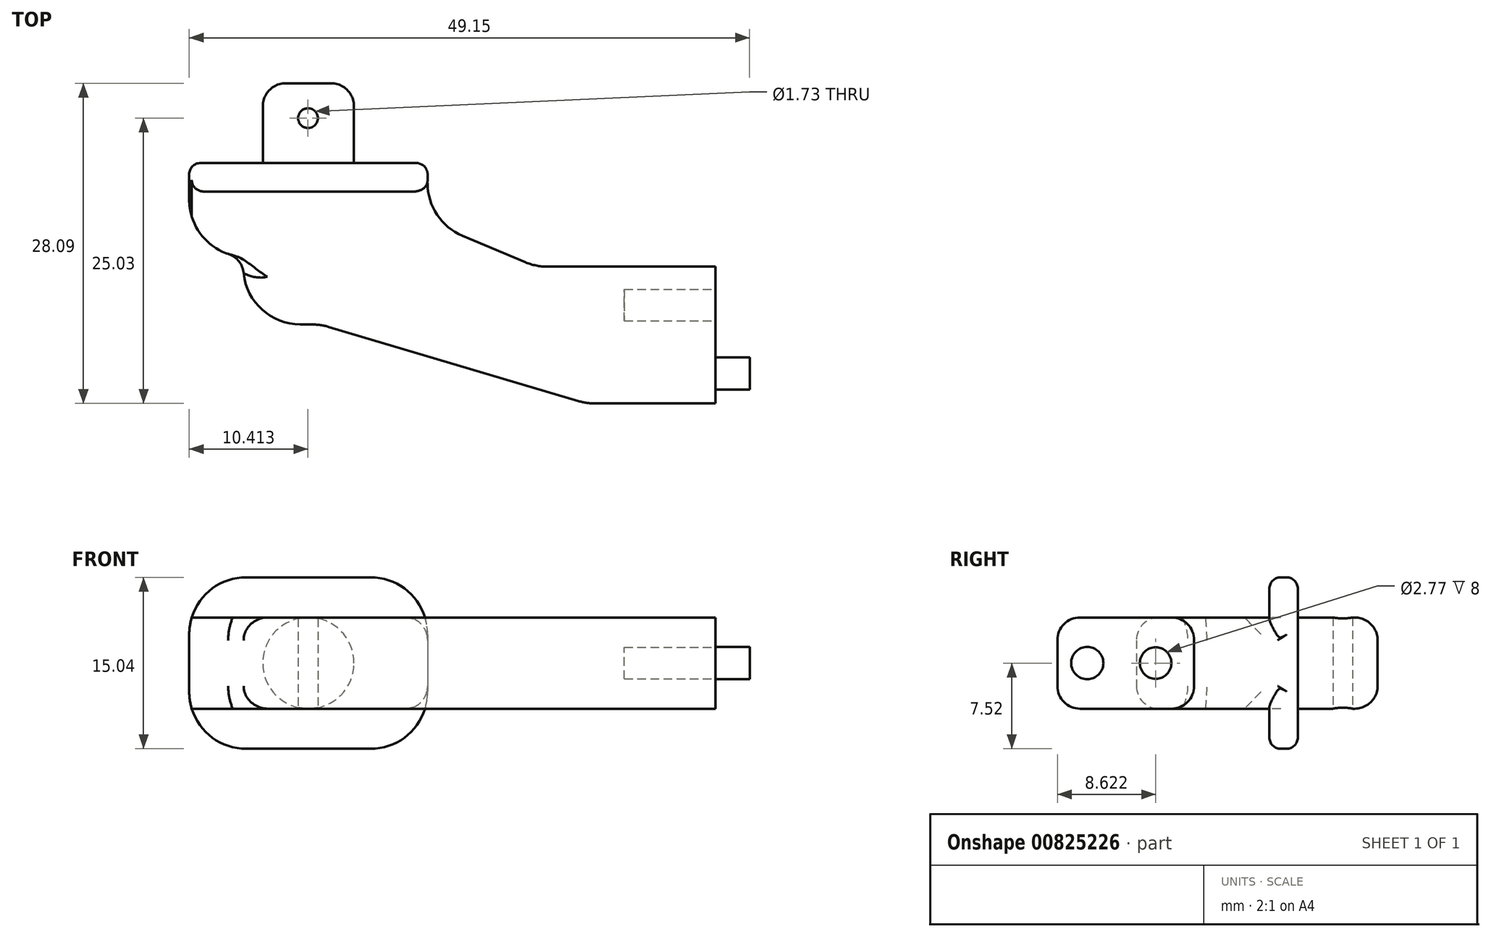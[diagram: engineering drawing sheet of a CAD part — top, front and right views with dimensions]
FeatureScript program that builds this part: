
annotation { "Feature Type Name" : "Feature", "Feature Type Description" : "" }
export const myFeature = defineFeature(function(context is Context, id is Id, definition is map)
    precondition{}
    {
        {
            var Q0;
            Q0=qCreatedBy(makeId("Top.planeOp"),FACE);
            var sketch = newSketch(context, id + "F0", { "sketchPlane" : qUnion([Q0])});
            skLineSegment(sketch, "E0.bottom", {"start": v(-29.76, 0) * mm, "end": v(-61.26, 0) * mm});
            skLineSegment(sketch, "E0.top", {"start": v(-29.76, 12) * mm, "end": v(-45.5, 12) * mm});
            skLineSegment(sketch, "E0.left", {"start": v(-29.76, 0) * mm, "end": v(-29.76, 12) * mm});
            skLineSegment(sketch, "E1", {"start": v(-61.26, 6) * mm, "end": v(-41.05, 0) * mm});
            skLineSegment(sketch, "E2", {"start": v(-45.5, 12) * mm, "end": v(-55, 16) * mm});
            skLineSegment(sketch, "E3", {"start": v(-75.91, 16) * mm, "end": v(-75.91, 12.87) * mm});
            skLineSegment(sketch, "E4", {"start": v(-75.91, 12.87) * mm, "end": v(-71.16, 12.87) * mm});
            skPoint(sketch, "E5.orphan", {"position": v(-61.26, 12) * mm});
            skLineSegment(sketch, "E6", {"start": v(-61.26, 6) * mm, "end": v(-64.38, 6.93) * mm});
            skLineSegment(sketch, "E7", {"start": v(-64.38, 6.93) * mm, "end": v(-71.16, 6.93) * mm});
            skLineSegment(sketch, "E8", {"start": v(-71.16, 6.93) * mm, "end": v(-71.16, 12.87) * mm});
            skLineSegment(sketch, "E9.top", {"start": v(-75.91, 21.1) * mm, "end": v(-55, 21.1) * mm});
            skLineSegment(sketch, "E9.left", {"start": v(-75.91, 16) * mm, "end": v(-75.91, 21.1) * mm});
            skLineSegment(sketch, "E9.right", {"start": v(-55, 16) * mm, "end": v(-55, 21.1) * mm});
            skPoint(sketch, "E10.end.orphan", {"position": v(-64.38, 6.34) * mm});
            skSolve(sketch);
        }
        {
            var Q0;
            Q0=makeQuery(id+"F0.imprint","IMPRINT",FACE,{"disambiguationData":[TD([[makeQuery(id+"F0.imprint","IMPRINT",EDGE,{"derivedFrom":sQuery(id+"F0.wireOp",EDGE,"E0.top")}),1.0]])]});
            extrude(context, id + "F1", {"entities" : qUnion([Q0]), "depth" : 8 * mm, "offsetDistance" : 25 * mm});
        }
        {
            var Q0;
            Q0=makeQuery(id+"F1.opExtrude","SWEPT_EDGE",EDGE,{"disambiguationData":[OSD([sQuery(id+"F0.wireOp",EDGE,"E3"),sQuery(id+"F0.wireOp",EDGE,"E4")])]});
            var Q1;
            Q1=makeQuery(id+"F1.opExtrude","SWEPT_EDGE",EDGE,{"disambiguationData":[OSD([sQuery(id+"F0.wireOp",EDGE,"E2"),sQuery(id+"F0.wireOp",EDGE,"E9.right")])]});
            var Q2;
            Q2=makeQuery(id+"F1.opExtrude","SWEPT_EDGE",EDGE,{"disambiguationData":[OSD([sQuery(id+"F0.wireOp",EDGE,"E0.top"),sQuery(id+"F0.wireOp",EDGE,"E2")])]});
            var Q3;
            Q3=makeQuery(id+"F1.opExtrude","SWEPT_EDGE",EDGE,{"disambiguationData":[OSD([sQuery(id+"F0.wireOp",EDGE,"E6"),sQuery(id+"F0.wireOp",EDGE,"E7")])]});
            var Q4;
            Q4=makeQuery(id+"F1.opExtrude","SWEPT_EDGE",EDGE,{"disambiguationData":[OSD([sQuery(id+"F0.wireOp",EDGE,"E0.bottom"),sQuery(id+"F0.wireOp",EDGE,"E1")])]});
            var Q5;
            Q5=makeQuery(id+"F1.opExtrude","SWEPT_EDGE",EDGE,{"disambiguationData":[OSD([sQuery(id+"F0.wireOp",EDGE,"E7"),sQuery(id+"F0.wireOp",EDGE,"E8")])]});
            fillet(context, id + "F2", {"entities" : qUnion([Q0, Q1, Q2, Q3, Q4, Q5]), "radius" : 5 * mm, "tangentPropagation" : true, "allowEdgeOverflow" : false});
        }
        {
            var Q0;
            Q0=makeQuery(id+"F1.opExtrude","SWEPT_FACE",FACE,{"disambiguationData":[OSD([sQuery(id+"F0.wireOp",EDGE,"E9.top")])]});
            var sketch = newSketch(context, id + "F3", { "sketchPlane" : qUnion([Q0])});
            skLineSegment(sketch, "E11.bottom", {"start": v(55, 8) * mm, "end": v(75.91, 8) * mm});
            skLineSegment(sketch, "E11.top", {"start": v(55, 11.52) * mm, "end": v(75.91, 11.52) * mm});
            skLineSegment(sketch, "E11.left", {"start": v(55, 8) * mm, "end": v(55, 11.52) * mm});
            skLineSegment(sketch, "E11.right", {"start": v(75.91, 8) * mm, "end": v(75.91, 11.52) * mm});
            skLineSegment(sketch, "E12.bottom", {"start": v(75.91, 0) * mm, "end": v(55, 0) * mm});
            skLineSegment(sketch, "E12.top", {"start": v(75.91, -3.52) * mm, "end": v(55, -3.52) * mm});
            skLineSegment(sketch, "E12.left", {"start": v(75.91, 0) * mm, "end": v(75.91, -3.52) * mm});
            skLineSegment(sketch, "E12.right", {"start": v(55, 0) * mm, "end": v(55, -3.52) * mm});
            skSolve(sketch);
        }
        {
            var Q0;
            Q0 = qSketchRegion(id + "F3", true);
            extrude(context, id + "F4", {"entities" : qUnion([Q0]), "operationType" : NewBodyOperationType.ADD, "oppositeDirection" : true, "depth" : 2.5 * mm, "offsetDistance" : 25 * mm});
        }
        {
            var Q0;
            Q0=makeQuery(id+"F4.opExtrude","SWEPT_EDGE",EDGE,{"disambiguationData":[OSD([sQuery(id+"F3.wireOp",EDGE,"E11.top"),sQuery(id+"F3.wireOp",EDGE,"E11.left")])]});
            var Q1;
            Q1=makeQuery(id+"F4.opExtrude","SWEPT_EDGE",EDGE,{"disambiguationData":[OSD([sQuery(id+"F3.wireOp",EDGE,"E12.top"),sQuery(id+"F3.wireOp",EDGE,"E12.right")])]});
            var Q2;
            Q2=makeQuery(id+"F4.opExtrude","SWEPT_EDGE",EDGE,{"disambiguationData":[OSD([sQuery(id+"F3.wireOp",EDGE,"E12.top"),sQuery(id+"F3.wireOp",EDGE,"E12.left")])]});
            var Q3;
            Q3=makeQuery(id+"F4.opExtrude","SWEPT_EDGE",EDGE,{"disambiguationData":[OSD([sQuery(id+"F3.wireOp",EDGE,"E11.top"),sQuery(id+"F3.wireOp",EDGE,"E11.right")])]});
            fillet(context, id + "F5", {"entities" : qUnion([Q0, Q1, Q2, Q3]), "radius" : 5 * mm, "tangentPropagation" : true, "allowEdgeOverflow" : false});
        }
        {
            var Q0;
            Q0=makeQuery(id+"F1.opExtrude","CAP_EDGE",EDGE,{"disambiguationData":[OSD([sQuery(id+"F0.wireOp",EDGE,"E0.top")])],"isStart":false});
            var Q1;
            Q1=makeQuery(id+"F1.opExtrude","CAP_EDGE",EDGE,{"disambiguationData":[OSD([sQuery(id+"F0.wireOp",EDGE,"E0.top")])],"isStart":true});
            var Q2;
            Q2=makeQuery(id+"F1.opExtrude","CAP_EDGE",EDGE,{"disambiguationData":[OSD([sQuery(id+"F0.wireOp",EDGE,"E1"),sQuery(id+"F0.wireOp",EDGE,"E6")])],"isStart":true});
            var Q3;
            Q3=makeQuery(id+"F1.opExtrude","CAP_EDGE",EDGE,{"disambiguationData":[OSD([sQuery(id+"F0.wireOp",EDGE,"E1"),sQuery(id+"F0.wireOp",EDGE,"E6")])],"isStart":false});
            fillet(context, id + "F6", {"entities" : qUnion([Q0, Q1, Q2, Q3]), "radius" : 2 * mm, "tangentPropagation" : true, "allowEdgeOverflow" : false});
        }
        {
            var Q0;
            Q0=makeQuery(id+"F2.opFillet","BLEND_EDGE",EDGE,{"blendedFrom":[makeQuery(id+"F1.opExtrude","SWEPT_EDGE",EDGE,{"disambiguationData":[OSD([sQuery(id+"F0.wireOp",EDGE,"E3"),sQuery(id+"F0.wireOp",EDGE,"E4")])]}),makeQuery(id+"F1.opExtrude","SWEPT_FACE",FACE,{"disambiguationData":[OSD([sQuery(id+"F0.wireOp",EDGE,"E8")])]})],"blendedInto":[makeQuery(id+"F1.opExtrude","SWEPT_FACE",FACE,{"disambiguationData":[OSD([sQuery(id+"F0.wireOp",EDGE,"E8")])]})]});
            var Q1;
            Q1=makeQuery(id+"F4.opExtrude","CAP_EDGE",EDGE,{"disambiguationData":[OSD([sQuery(id+"F3.wireOp",EDGE,"E11.bottom")])],"isStart":false});
            var Q2;
            Q2=makeQuery(id+"F4.opExtrude","CAP_EDGE",EDGE,{"disambiguationData":[OSD([sQuery(id+"F3.wireOp",EDGE,"E12.bottom")])],"isStart":false});
            fillet(context, id + "F7", {"entities" : qUnion([Q0, Q1, Q2]), "radius" : 2 * mm, "tangentPropagation" : true, "allowEdgeOverflow" : false});
        }
        {
            var Q0;
            Q0=makeQuery(id+"F4.boolean.opBoolean","MERGE",FACE,{"derivedFrom":[makeQuery(id+"F1.opExtrude","SWEPT_FACE",FACE,{"disambiguationData":[OSD([sQuery(id+"F0.wireOp",EDGE,"E9.top")])]}),makeQuery(id+"F4.opExtrude","CAP_FACE",FACE,{"disambiguationData":[OSD([sQuery(id+"F3.wireOp",EDGE,"E11.bottom"),sQuery(id+"F3.wireOp",EDGE,"E11.top"),sQuery(id+"F3.wireOp",EDGE,"E11.left"),sQuery(id+"F3.wireOp",EDGE,"E11.right")])],"isStart":true}),makeQuery(id+"F4.opExtrude","CAP_FACE",FACE,{"disambiguationData":[OSD([sQuery(id+"F3.wireOp",EDGE,"E12.bottom"),sQuery(id+"F3.wireOp",EDGE,"E12.top"),sQuery(id+"F3.wireOp",EDGE,"E12.left"),sQuery(id+"F3.wireOp",EDGE,"E12.right")])],"isStart":true})]});
            var sketch = newSketch(context, id + "F8", { "sketchPlane" : qUnion([Q0])});
            skCircle(sketch, "E13", {"center": v(65.46, 4) * mm, "radius": 4 * mm});
            skPoint(sketch, "E13.centerSnap0", {"position": v(65.46, 11.52) * mm});
            skPoint(sketch, "E13.centerSnap1", {"position": v(55, 4) * mm});
            skSolve(sketch);
        }
        {
            var Q0;
            Q0 = qSketchRegion(id + "F8", true);
            extrude(context, id + "F9", {"entities" : qUnion([Q0]), "operationType" : NewBodyOperationType.ADD, "depth" : 7 * mm, "offsetDistance" : 25 * mm});
        }
        {
            var Q0;
            Q0=makeQuery(id+"F9.opExtrude","CAP_EDGE",EDGE,{"disambiguationData":[OSD([sQuery(id+"F8.wireOp",EDGE,"E13")])],"isStart":false});
            fillet(context, id + "F10", {"entities" : qUnion([Q0]), "radius" : 2 * mm, "tangentPropagation" : true, "allowEdgeOverflow" : false});
        }
        {
            var Q0;
            Q0=qCreatedBy(makeId("Top.planeOp"),FACE);
            var sketch = newSketch(context, id + "F11", { "sketchPlane" : qUnion([Q0])});
            skCircle(sketch, "E14", {"center": v(-65.5, 25.03) * mm, "radius": 0.87 * mm});
            skSolve(sketch);
        }
        {
            var Q0;
            Q0 = qSketchRegion(id + "F11", true);
            extrude(context, id + "F12", {"entities" : qUnion([Q0]), "operationType" : NewBodyOperationType.REMOVE, "depth" : 25 * mm, "offsetDistance" : 25 * mm});
        }
        {
            var Q0;
            Q0=makeQuery(id+"F12.boolean.opBoolean","COPY",FACE,{"derivedFrom":makeQuery(id+"F12.opExtrude","CAP_FACE",FACE,{"disambiguationData":[OSD([sQuery(id+"F11.wireOp",EDGE,"E14")])],"isStart":true})});
            extrude(context, id + "F13", {"entities" : qUnion([Q0]), "operationType" : NewBodyOperationType.REMOVE, "oppositeDirection" : true, "depth" : 25 * mm, "offsetDistance" : 25 * mm});
        }
        {
            var Q0;
            Q0=makeQuery(id+"F9.opExtrude","CAP_EDGE",EDGE,{"disambiguationData":[OSD([sQuery(id+"F8.wireOp",EDGE,"E13")])],"isStart":true});
            var Q1;
            Q1=makeQuery(id+"F4.opExtrude","CAP_EDGE",EDGE,{"disambiguationData":[OSD([sQuery(id+"F3.wireOp",EDGE,"E12.top")])],"isStart":true});
            fillet(context, id + "F14", {"entities" : qUnion([Q0, Q1]), "radius" : 1 * mm, "tangentPropagation" : true, "allowEdgeOverflow" : false});
        }
        {
            var Q0;
            Q0=makeQuery(id+"F1.opExtrude","SWEPT_FACE",FACE,{"disambiguationData":[OSD([sQuery(id+"F0.wireOp",EDGE,"E0.left")])]});
            var sketch = newSketch(context, id + "F15", { "sketchPlane" : qUnion([Q0])});
            skCircle(sketch, "E15", {"center": v(8.62, 4) * mm, "radius": 1.39 * mm});
            skPoint(sketch, "E15.centerSnap0", {"position": v(12, 4) * mm});
            skCircle(sketch, "E16", {"center": v(2.62, 4) * mm, "radius": 1.33 * mm});
            skSolve(sketch);
        }
        {
            var Q0;
            Q0=makeQuery(id+"F15.imprint","IMPRINT",FACE,{"disambiguationData":[TD([[makeQuery(id+"F15.imprint","IMPRINT",EDGE,{"derivedFrom":sQuery(id+"F15.wireOp",EDGE,"E15")}),1.0]])]});
            extrude(context, id + "F16", {"entities" : qUnion([Q0]), "operationType" : NewBodyOperationType.REMOVE, "oppositeDirection" : true, "depth" : 8 * mm, "offsetDistance" : 25 * mm});
        }
        {
            var Q0;
            Q0=makeQuery(id+"F1.opExtrude","SWEPT_FACE",FACE,{"disambiguationData":[OSD([sQuery(id+"F0.wireOp",EDGE,"E0.left")])]});
            var sketch = newSketch(context, id + "F17", { "sketchPlane" : qUnion([Q0])});
            skCircle(sketch, "E17", {"center": v(2.62, 4) * mm, "radius": 1.41 * mm});
            skPoint(sketch, "E18.center.orphan", {"position": v(8.62, 4) * mm});
            skSolve(sketch);
        }
        {
            var Q0;
            Q0 = qSketchRegion(id + "F17", true);
            extrude(context, id + "F18", {"entities" : qUnion([Q0]), "operationType" : NewBodyOperationType.ADD, "depth" : 3 * mm, "offsetDistance" : 25 * mm});
        }
        {
            var Q0;
            Q0=makeQuery(id+"F4.opExtrude","CAP_EDGE",EDGE,{"disambiguationData":[OSD([sQuery(id+"F3.wireOp",EDGE,"E12.top")])],"isStart":false});
            var Q1;
            Q1=makeQuery(id+"F4.opExtrude","CAP_EDGE",EDGE,{"disambiguationData":[OSD([sQuery(id+"F3.wireOp",EDGE,"E11.top")])],"isStart":false});
            fillet(context, id + "F19", {"entities" : qUnion([Q0, Q1]), "radius" : 1 * mm, "tangentPropagation" : true, "allowEdgeOverflow" : false});
        }
    });
